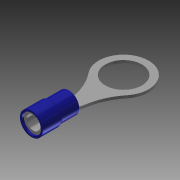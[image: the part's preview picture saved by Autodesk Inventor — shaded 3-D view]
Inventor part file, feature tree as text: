
AUTODESK INVENTOR PART (.ipt)
format: ipt  version: 2014 (Build 180170000, 170)  size: 272,384 bytes
history: native  units: in
note: dims shown in document units (in); Inventor stores cm internally (conversion verified against a paired STEP export)
features: sketch x5, projected_geometry x4, extrude x3, fillet x3, shell x1, revolve x1, plane x1, loft x1, chamfer x1, other x1
ambient origin geometry x8: Origin, YZ Plane, XZ Plane, XY Plane, X Axis, Y Axis, Z Axis, Center Point
bodies: Solid1 (feature_tree), Solid2 (feature_tree)
feature tree (21):
  extrude  "Extrusion1"  Depth=0.4in TaperAngle=0.0deg
  extrude  "Extrusion2"  Depth=0.209in TaperAngle=0.0deg
  fillet  "Fillet1"  Radius=0.005in
  fillet  "Fillet2"  Radius=0.02in
  shell  "Shell1"  Thickness=0.02in
  revolve  "Revolution1"  [1 undecoded]
  plane  "Work Plane1"
  extrude  "Extrusion3"  [1 undecoded]
  loft  "Loft1"
  fillet  "Fillet3"  Radius=0.0715in
  chamfer  "Chamfer1"  Distance=0.099in
  sketch  "Sketch1"  dims[d0=0.223in d1=0.4in d2=0.0in]
  sketch  "Sketch2"  dims[d3=0.245in d4=0.209in d5=0.0in d6=0.005in d7=0.02in d8=0.02in]
  projected_geometry  "Projected Loop1"
  sketch  "Sketch3"  dims[d9=0.0285in d10=0.0285in]
  sketch  "Sketch4"  dims[d11=90.0deg d12=-0.069in]
  sketch  "Sketch5"  dims[d13=0.587in d14=0.534in d15=0.0715in d16=0.099in d17=0.0285in d18=0.0in d19=0.0in d20=90.0deg d21=0.3937in d22=90.0deg d23=0.02in d24=0.003in d25=0.125in d26=45.0deg]
  projected_geometry  "Projected Loop2"
  other  "Edges1"
  projected_geometry  "Project Cut Edges1"
  projected_geometry  "Project Cut Edges2"
note: 2 required parameter values undecoded (feature->parameter linkage not recoverable at this tier; creation-order binding heuristic only, values carry confidence <= 0.55)